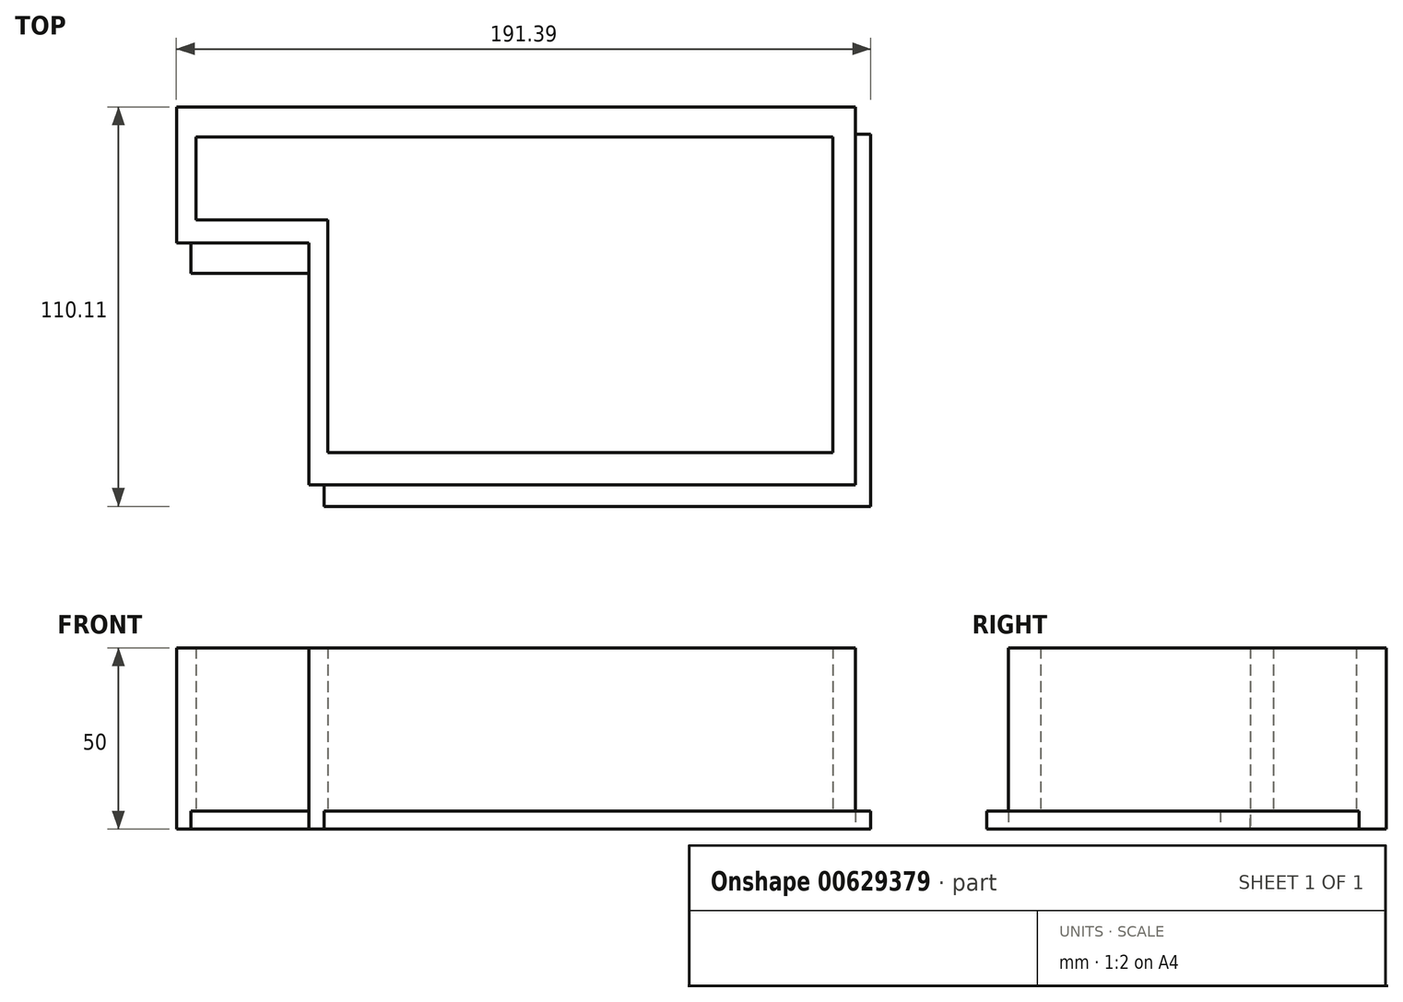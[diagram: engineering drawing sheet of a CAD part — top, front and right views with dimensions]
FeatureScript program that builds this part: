
annotation { "Feature Type Name" : "Feature", "Feature Type Description" : "" }
export const myFeature = defineFeature(function(context is Context, id is Id, definition is map)
    precondition{}
    {
        {
            var Q0;
            Q0=qCreatedBy(makeId("Top.planeOp"),FACE);
            var sketch = newSketch(context, id + "F0", { "sketchPlane" : qUnion([Q0])});
            skLineSegment(sketch, "E0.bottom", {"start": v(-95.6, 51.22) * mm, "end": v(55.06, 51.22) * mm});
            skLineSegment(sketch, "E0.top", {"start": v(-95.6, -51.31) * mm, "end": v(55.06, -51.31) * mm});
            skLineSegment(sketch, "E0.left", {"start": v(-95.6, 51.22) * mm, "end": v(-95.6, -51.31) * mm});
            skLineSegment(sketch, "E0.right", {"start": v(55.06, 51.22) * mm, "end": v(55.06, -51.31) * mm});
            skLineSegment(sketch, "E1.bottom", {"start": v(-95.6, 51.22) * mm, "end": v(-132.3, 51.22) * mm});
            skLineSegment(sketch, "E1.top", {"start": v(-95.6, 12.96) * mm, "end": v(-132.3, 12.96) * mm});
            skLineSegment(sketch, "E1.left", {"start": v(-95.6, 51.22) * mm, "end": v(-95.6, 12.96) * mm});
            skLineSegment(sketch, "E1.right", {"start": v(-132.3, 51.22) * mm, "end": v(-132.3, 12.96) * mm});
            skSolve(sketch);
        }
        {
            var Q0;
            Q0 = qSketchRegion(id + "F0", true);
            extrude(context, id + "F1", {"entities" : qUnion([Q0]), "depth" : 5 * mm, "offsetDistance" : 25.4 * mm});
        }
        {
            var Q0;
            Q0=qCreatedBy(makeId("Top.planeOp"),FACE);
            var sketch = newSketch(context, id + "F2", { "sketchPlane" : qUnion([Q0])});
            skLineSegment(sketch, "E2.bottom", {"start": v(-136.33, 58.8) * mm, "end": v(50.83, 58.8) * mm});
            skLineSegment(sketch, "E2.top", {"start": v(-136.33, 50.47) * mm, "end": v(50.83, 50.47) * mm});
            skLineSegment(sketch, "E2.left", {"start": v(-136.33, 58.8) * mm, "end": v(-136.33, 50.47) * mm});
            skLineSegment(sketch, "E2.right", {"start": v(50.83, 58.8) * mm, "end": v(50.83, 50.47) * mm});
            skLineSegment(sketch, "E3.bottom", {"start": v(50.83, 50.47) * mm, "end": v(44.54, 50.47) * mm});
            skLineSegment(sketch, "E3.top", {"start": v(50.83, -45.41) * mm, "end": v(44.54, -45.41) * mm});
            skLineSegment(sketch, "E3.left", {"start": v(50.83, 50.47) * mm, "end": v(50.83, -45.41) * mm});
            skLineSegment(sketch, "E3.right", {"start": v(44.54, 50.47) * mm, "end": v(44.54, -45.41) * mm});
            skLineSegment(sketch, "E4.bottom", {"start": v(50.83, -45.41) * mm, "end": v(-99.83, -45.41) * mm});
            skLineSegment(sketch, "E4.top", {"start": v(50.83, -36.52) * mm, "end": v(-99.83, -36.52) * mm});
            skLineSegment(sketch, "E4.left", {"start": v(50.83, -45.41) * mm, "end": v(50.83, -36.52) * mm});
            skLineSegment(sketch, "E4.right", {"start": v(-99.83, -45.41) * mm, "end": v(-99.83, -36.52) * mm});
            skLineSegment(sketch, "E5.bottom", {"start": v(-99.83, -45.41) * mm, "end": v(-94.65, -45.41) * mm});
            skLineSegment(sketch, "E5.top", {"start": v(-99.83, 27.68) * mm, "end": v(-94.65, 27.68) * mm});
            skLineSegment(sketch, "E5.left", {"start": v(-99.83, -45.41) * mm, "end": v(-99.83, 27.68) * mm});
            skLineSegment(sketch, "E5.right", {"start": v(-94.65, -45.41) * mm, "end": v(-94.65, 27.68) * mm});
            skLineSegment(sketch, "E6.bottom", {"start": v(-136.33, 21.3) * mm, "end": v(-94.65, 21.3) * mm});
            skLineSegment(sketch, "E6.top", {"start": v(-136.33, 27.68) * mm, "end": v(-94.65, 27.68) * mm});
            skLineSegment(sketch, "E6.left", {"start": v(-136.33, 21.3) * mm, "end": v(-136.33, 27.68) * mm});
            skLineSegment(sketch, "E6.right", {"start": v(-94.65, 21.3) * mm, "end": v(-94.65, 27.68) * mm});
            skLineSegment(sketch, "E7.bottom", {"start": v(-136.33, 27.68) * mm, "end": v(-130.95, 27.68) * mm});
            skLineSegment(sketch, "E7.top", {"start": v(-136.33, 58.8) * mm, "end": v(-130.95, 58.8) * mm});
            skLineSegment(sketch, "E7.left", {"start": v(-136.33, 27.68) * mm, "end": v(-136.33, 58.8) * mm});
            skLineSegment(sketch, "E7.right", {"start": v(-130.95, 27.68) * mm, "end": v(-130.95, 58.8) * mm});
            skSolve(sketch);
        }
        {
            var Q0;
            Q0 = qSketchRegion(id + "F2", true);
            extrude(context, id + "F3", {"entities" : qUnion([Q0]), "operationType" : NewBodyOperationType.ADD, "depth" : 50 * mm, "offsetDistance" : 25 * mm});
        }
    });
